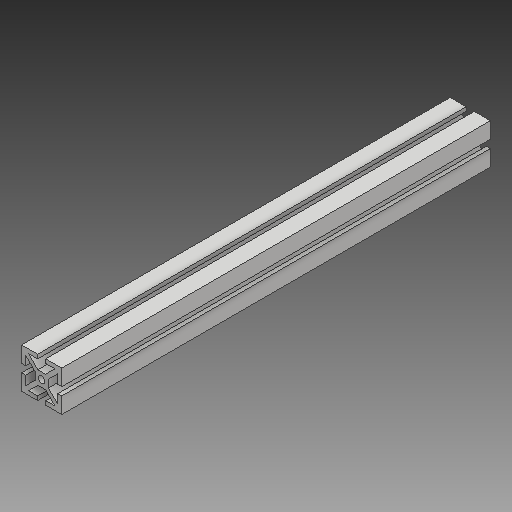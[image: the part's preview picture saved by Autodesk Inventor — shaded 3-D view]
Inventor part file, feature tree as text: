
AUTODESK INVENTOR PART (.ipt)
format: ipt  version: 2018 (Build 220112000, 112)  size: 150,528 bytes
history: native  units: mm
features: extrude x1, sketch x1
ambient origin geometry x8: Origin, YZ Plane, XZ Plane, XY Plane, X Axis, Y Axis, Z Axis, Center Point
bodies: Volumenkörper1 (feature_tree)
feature tree (2):
  extrude  "Extrusion1"  Depth=3.0mm
  sketch  "Skizze1"  dims[d0=3.0mm d1=3.0mm d2=0.5mm d3=1.0mm d4=1.0mm d5=1.2mm d6=1.2mm d7=1.2mm d8=1.2mm d9=0.3mm d10=0.15mm d11=0.15mm d12=0.15mm d13=0.15mm d14=32.0mm d15=0.0mm]
